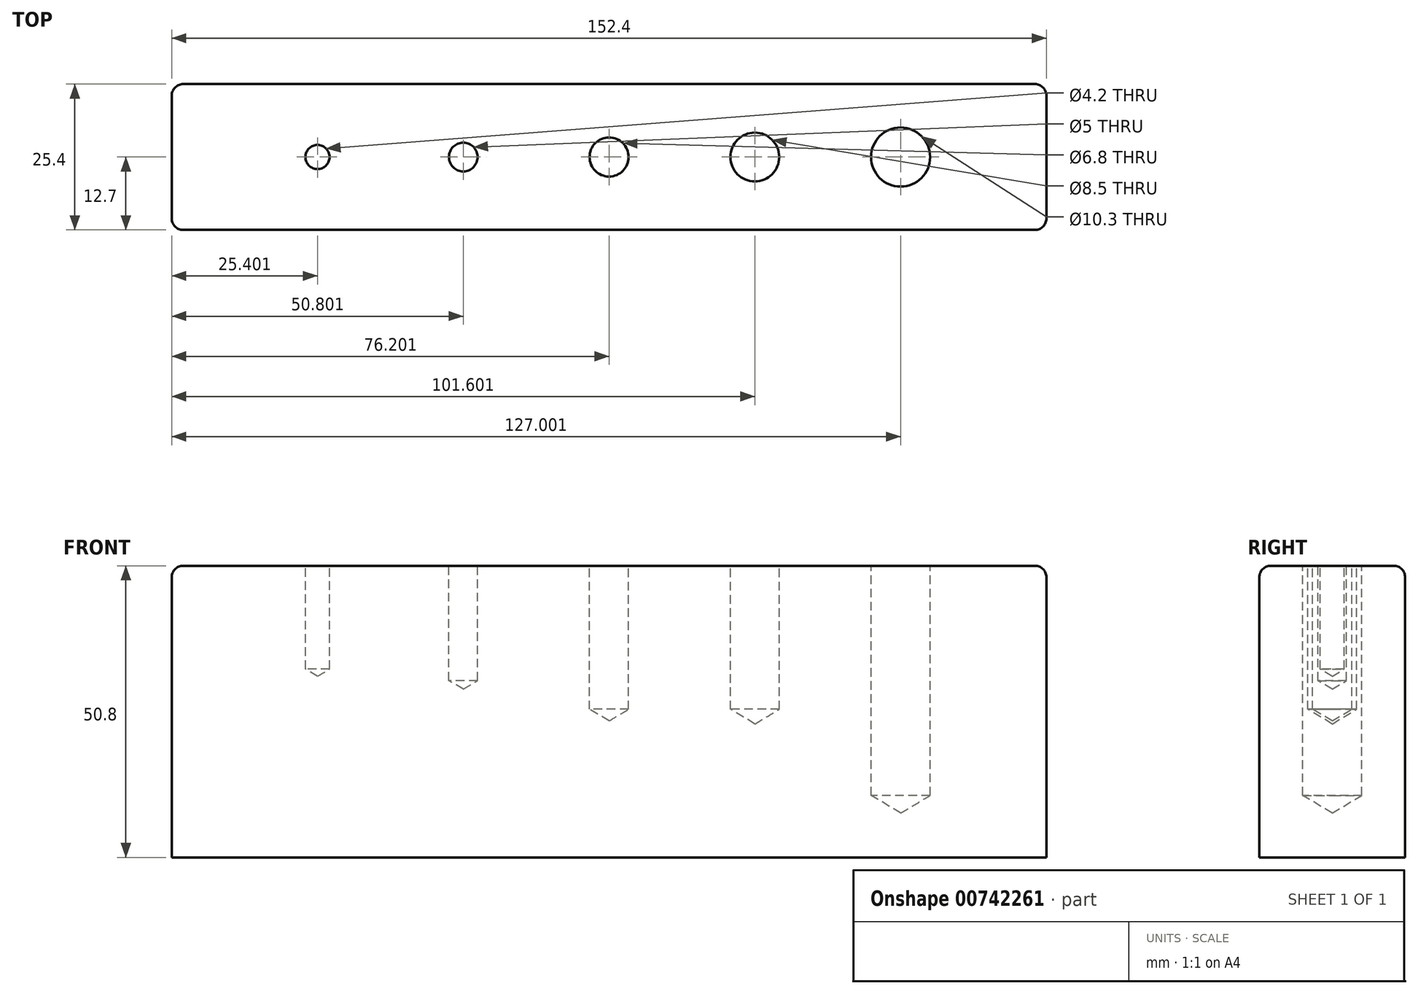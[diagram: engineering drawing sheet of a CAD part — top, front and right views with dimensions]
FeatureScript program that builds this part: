
annotation { "Feature Type Name" : "Feature", "Feature Type Description" : "" }
export const myFeature = defineFeature(function(context is Context, id is Id, definition is map)
    precondition{}
    {
        {
            var Q0;
            Q0=qCreatedBy(makeId("Top.planeOp"),FACE);
            var sketch = newSketch(context, id + "F0", { "sketchPlane" : qUnion([Q0])});
            skLineSegment(sketch, "E0.bottom", {"start": v(-54.1, 12.7) * mm, "end": v(98.3, 12.7) * mm});
            skLineSegment(sketch, "E0.top", {"start": v(-54.1, -12.7) * mm, "end": v(98.3, -12.7) * mm});
            skLineSegment(sketch, "E0.left", {"start": v(-54.1, 12.7) * mm, "end": v(-54.1, -12.7) * mm});
            skLineSegment(sketch, "E0.right", {"start": v(98.3, 12.7) * mm, "end": v(98.3, -12.7) * mm});
            skPoint(sketch, "E1", {"position": v(72.9, 0) * mm});
            skPoint(sketch, "E2", {"position": v(47.5, 0) * mm});
            skPoint(sketch, "E3", {"position": v(22.1, 0) * mm});
            skPoint(sketch, "E4", {"position": v(-3.3, 0) * mm});
            skPoint(sketch, "E5", {"position": v(-28.7, 0) * mm});
            skSolve(sketch);
        }
        {
            var Q0;
            Q0=makeQuery(id+"F0.imprint","IMPRINT",FACE,{"disambiguationData":[TD([[makeQuery(id+"F0.imprint","IMPRINT",EDGE,{"derivedFrom":sQuery(id+"F0.wireOp",EDGE,"E0.bottom")}),-1.0]])]});
            extrude(context, id + "F1", {"entities" : qUnion([Q0]), "oppositeDirection" : true, "depth" : 50.8 * mm, "offsetDistance" : 25.4 * mm});
        }
        {
            var Q0;
            Q0=sQuery(id+"F0.wireOp",VERTEX,"E5");
            var Q1;
            Q1=makeQuery(id+"F1.opExtrude","SWEPT_BODY",BODY,{"disambiguationData":[OSD([sQuery(id+"F0.wireOp",EDGE,"E0.bottom"),sQuery(id+"F0.wireOp",EDGE,"E0.top"),sQuery(id+"F0.wireOp",EDGE,"E0.left"),sQuery(id+"F0.wireOp",EDGE,"E0.right")])]});
            hole(context, id + "F2", {"style" : HoleStyle.SIMPLE, "endStyle" : HoleEndStyle.BLIND, "standardTappedOrClearance" : lookupTablePath({ "standard" : "ISO", "engagement" : "75%", "pitch" : "0.8 mm", "size" : "M5", "type" : "Tapped" }), "standardBlindInLast" : lookupTablePath({ "standard" : "ISO", "engagement" : "75%", "pitch" : "0.8 mm", "size" : "M5", "type" : "Tapped" }), "holeDiameter" : 4.2 * mm, "majorDiameter" : 5 * mm, "showTappedDepth" : true, "holeDepth" : 18 * mm, "isTappedThrough" : true, "tappedDepth" : 15.6 * mm, "tapClearance" : 3, "locations" : qUnion([Q0]), "scope" : qUnion([Q1])});
        }
        {
            var Q0;
            Q0=sQuery(id+"F0.wireOp",VERTEX,"E4");
            var Q1;
            Q1=makeQuery(id+"F1.opExtrude","SWEPT_BODY",BODY,{"disambiguationData":[OSD([sQuery(id+"F0.wireOp",EDGE,"E0.bottom"),sQuery(id+"F0.wireOp",EDGE,"E0.top"),sQuery(id+"F0.wireOp",EDGE,"E0.left"),sQuery(id+"F0.wireOp",EDGE,"E0.right")])]});
            hole(context, id + "F3", {"style" : HoleStyle.SIMPLE, "endStyle" : HoleEndStyle.BLIND, "standardTappedOrClearance" : lookupTablePath({ "standard" : "ISO", "engagement" : "75%", "pitch" : "1 mm", "size" : "M6", "type" : "Tapped" }), "standardBlindInLast" : lookupTablePath({ "standard" : "ISO", "engagement" : "75%", "pitch" : "1 mm", "size" : "M6", "type" : "Tapped" }), "holeDiameter" : 5 * mm, "majorDiameter" : 6 * mm, "showTappedDepth" : true, "holeDepth" : 20 * mm, "isTappedThrough" : true, "tappedDepth" : 17 * mm, "tapClearance" : 3, "locations" : qUnion([Q0]), "scope" : qUnion([Q1])});
        }
        {
            var Q0;
            Q0=sQuery(id+"F0.wireOp",VERTEX,"E3");
            var Q1;
            Q1=makeQuery(id+"F1.opExtrude","SWEPT_BODY",BODY,{"disambiguationData":[OSD([sQuery(id+"F0.wireOp",EDGE,"E0.bottom"),sQuery(id+"F0.wireOp",EDGE,"E0.top"),sQuery(id+"F0.wireOp",EDGE,"E0.left"),sQuery(id+"F0.wireOp",EDGE,"E0.right")])]});
            hole(context, id + "F4", {"style" : HoleStyle.SIMPLE, "endStyle" : HoleEndStyle.BLIND, "standardTappedOrClearance" : lookupTablePath({ "standard" : "ISO", "engagement" : "75%", "pitch" : "1.25 mm", "size" : "M8", "type" : "Tapped" }), "standardBlindInLast" : lookupTablePath({ "standard" : "ISO", "engagement" : "75%", "pitch" : "1.25 mm", "size" : "M8", "type" : "Tapped" }), "holeDiameter" : 6.8 * mm, "majorDiameter" : 8 * mm, "showTappedDepth" : true, "holeDepth" : 25 * mm, "isTappedThrough" : true, "tappedDepth" : 21.25 * mm, "tapClearance" : 3, "locations" : qUnion([Q0]), "scope" : qUnion([Q1])});
        }
        {
            var Q0;
            Q0=sQuery(id+"F0.wireOp",VERTEX,"E2");
            var Q1;
            Q1=makeQuery(id+"F1.opExtrude","SWEPT_BODY",BODY,{"disambiguationData":[OSD([sQuery(id+"F0.wireOp",EDGE,"E0.bottom"),sQuery(id+"F0.wireOp",EDGE,"E0.top"),sQuery(id+"F0.wireOp",EDGE,"E0.left"),sQuery(id+"F0.wireOp",EDGE,"E0.right")])]});
            hole(context, id + "F5", {"style" : HoleStyle.SIMPLE, "endStyle" : HoleEndStyle.BLIND, "standardTappedOrClearance" : lookupTablePath({ "standard" : "ISO", "engagement" : "75%", "pitch" : "1.5 mm", "size" : "M10", "type" : "Tapped" }), "standardBlindInLast" : lookupTablePath({ "standard" : "ISO", "engagement" : "75%", "pitch" : "1.5 mm", "size" : "M10", "type" : "Tapped" }), "holeDiameter" : 8.5 * mm, "majorDiameter" : 10 * mm, "showTappedDepth" : true, "holeDepth" : 25 * mm, "isTappedThrough" : true, "tappedDepth" : 20.5 * mm, "tapClearance" : 3, "locations" : qUnion([Q0]), "scope" : qUnion([Q1])});
        }
        {
            var Q0;
            Q0=sQuery(id+"F0.wireOp",VERTEX,"E1");
            var Q1;
            Q1=makeQuery(id+"F1.opExtrude","SWEPT_BODY",BODY,{"disambiguationData":[OSD([sQuery(id+"F0.wireOp",EDGE,"E0.bottom"),sQuery(id+"F0.wireOp",EDGE,"E0.top"),sQuery(id+"F0.wireOp",EDGE,"E0.left"),sQuery(id+"F0.wireOp",EDGE,"E0.right")])]});
            hole(context, id + "F6", {"style" : HoleStyle.SIMPLE, "endStyle" : HoleEndStyle.BLIND, "standardTappedOrClearance" : lookupTablePath({ "standard" : "ISO", "engagement" : "75%", "pitch" : "1.75 mm", "size" : "M12", "type" : "Tapped" }), "standardBlindInLast" : lookupTablePath({ "standard" : "ISO", "engagement" : "75%", "pitch" : "1.75 mm", "size" : "M12", "type" : "Tapped" }), "holeDiameter" : 10.3 * mm, "majorDiameter" : 12 * mm, "showTappedDepth" : true, "holeDepth" : 40 * mm, "isTappedThrough" : true, "tappedDepth" : 34.75 * mm, "tapClearance" : 3, "locations" : qUnion([Q0]), "scope" : qUnion([Q1])});
        }
        {
            var Q0;
            Q0=makeQuery(id+"F1.opExtrude","CAP_EDGE",EDGE,{"disambiguationData":[OSD([sQuery(id+"F0.wireOp",EDGE,"E0.top")])],"isStart":true});
            var Q1;
            Q1=makeQuery(id+"F1.opExtrude","CAP_EDGE",EDGE,{"disambiguationData":[OSD([sQuery(id+"F0.wireOp",EDGE,"E0.right")])],"isStart":true});
            var Q2;
            Q2=makeQuery(id+"F1.opExtrude","CAP_EDGE",EDGE,{"disambiguationData":[OSD([sQuery(id+"F0.wireOp",EDGE,"E0.bottom")])],"isStart":true});
            var Q3;
            Q3=makeQuery(id+"F1.opExtrude","CAP_EDGE",EDGE,{"disambiguationData":[OSD([sQuery(id+"F0.wireOp",EDGE,"E0.left")])],"isStart":true});
            var Q4;
            Q4=makeQuery(id+"F1.opExtrude","SWEPT_EDGE",EDGE,{"disambiguationData":[OSD([sQuery(id+"F0.wireOp",EDGE,"E0.bottom"),sQuery(id+"F0.wireOp",EDGE,"E0.right")])]});
            var Q5;
            Q5=makeQuery(id+"F1.opExtrude","SWEPT_EDGE",EDGE,{"disambiguationData":[OSD([sQuery(id+"F0.wireOp",EDGE,"E0.top"),sQuery(id+"F0.wireOp",EDGE,"E0.right")])]});
            var Q6;
            Q6=makeQuery(id+"F1.opExtrude","SWEPT_EDGE",EDGE,{"disambiguationData":[OSD([sQuery(id+"F0.wireOp",EDGE,"E0.bottom"),sQuery(id+"F0.wireOp",EDGE,"E0.left")])]});
            var Q7;
            Q7=makeQuery(id+"F1.opExtrude","SWEPT_EDGE",EDGE,{"disambiguationData":[OSD([sQuery(id+"F0.wireOp",EDGE,"E0.top"),sQuery(id+"F0.wireOp",EDGE,"E0.left")])]});
            fillet(context, id + "F7", {"entities" : qUnion([Q0, Q1, Q2, Q3, Q4, Q5, Q6, Q7]), "radius" : 2 * mm, "tangentPropagation" : true, "allowEdgeOverflow" : false});
        }
    });
